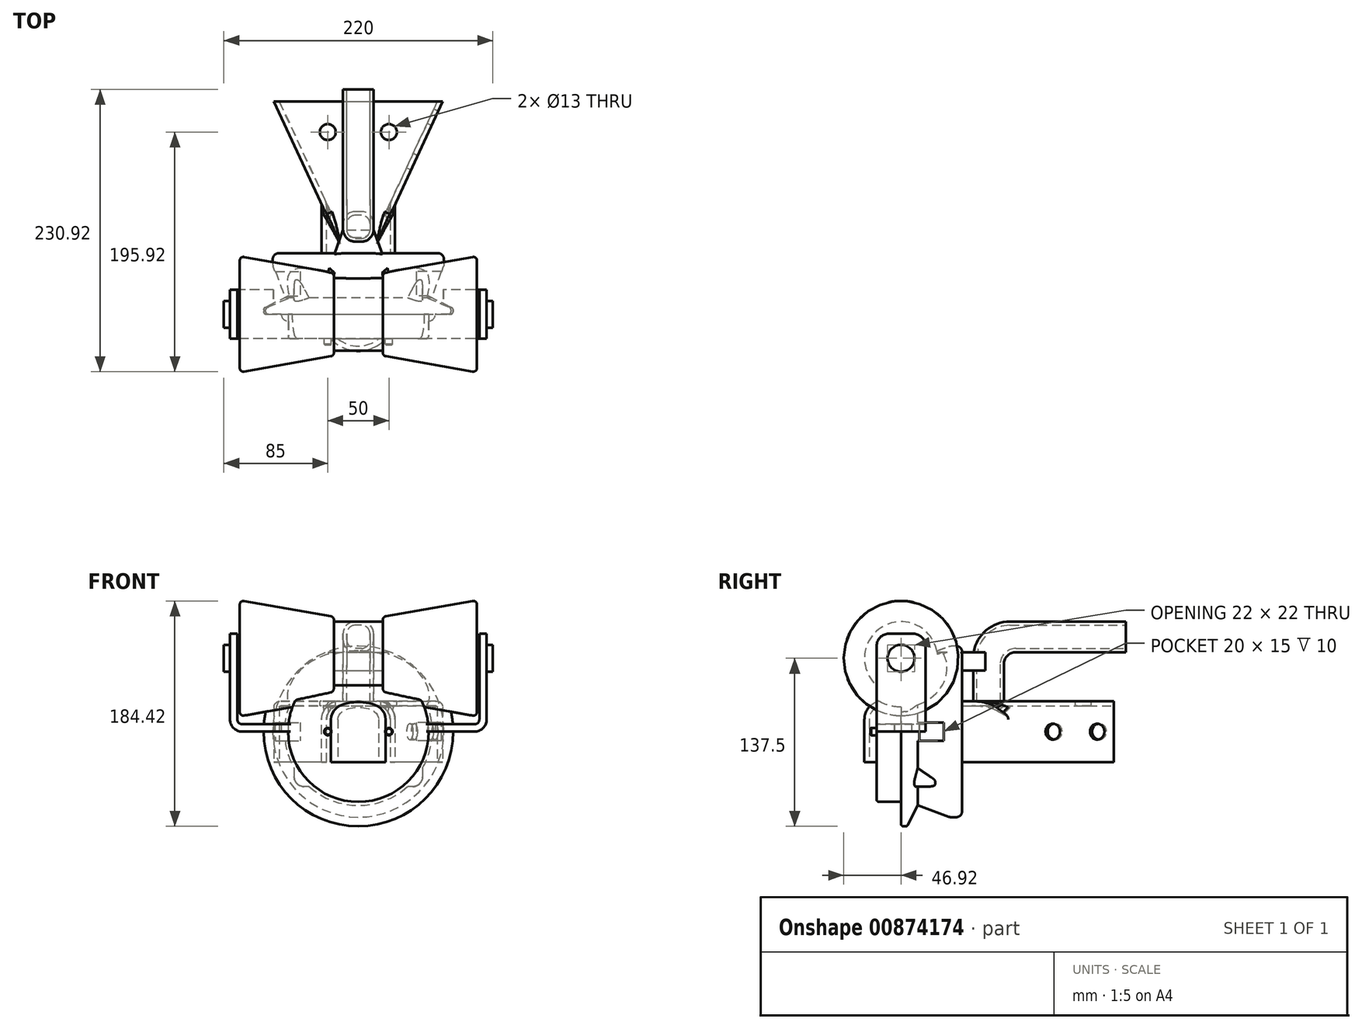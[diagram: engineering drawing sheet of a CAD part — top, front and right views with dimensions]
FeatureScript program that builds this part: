
annotation { "Feature Type Name" : "Feature", "Feature Type Description" : "" }
export const myFeature = defineFeature(function(context is Context, id is Id, definition is map)
    precondition{}
    {
        {
            var Q0;
            Q0=qCreatedBy(makeId("Front.planeOp"),FACE);
            var sketch = newSketch(context, id + "F0", { "sketchPlane" : qUnion([Q0])});
            skLineSegment(sketch, "E0.bottom", {"start": v(-52.5, -45) * mm, "end": v(52.5, -45) * mm});
            skLineSegment(sketch, "E0.top", {"start": v(-52.5, 45) * mm, "end": v(52.5, 45) * mm});
            skLineSegment(sketch, "E0.left", {"start": v(-52.5, -45) * mm, "end": v(-52.5, 45) * mm});
            skLineSegment(sketch, "E0.right", {"start": v(52.5, -45) * mm, "end": v(52.5, 45) * mm});
            skPoint(sketch, "E0.middle", {"position": v(0, 0) * mm});
            skSolve(sketch);
        }
        {
            var Q0;
            Q0 = qSketchRegion(id + "F0", true);
            extrude(context, id + "F1", {"entities" : qUnion([Q0]), "oppositeDirection" : true, "depth" : 30 * mm, "offsetDistance" : 25 * mm});
        }
        {
            var Q0;
            Q0=makeQuery(id+"F1.opExtrude","SWEPT_EDGE",EDGE,{"disambiguationData":[OSD([sQuery(id+"F0.wireOp",EDGE,"E0.top"),sQuery(id+"F0.wireOp",EDGE,"E0.right")])]});
            var Q1;
            Q1=makeQuery(id+"F1.opExtrude","SWEPT_EDGE",EDGE,{"disambiguationData":[OSD([sQuery(id+"F0.wireOp",EDGE,"E0.top"),sQuery(id+"F0.wireOp",EDGE,"E0.left")])]});
            var Q2;
            Q2=makeQuery(id+"F1.opExtrude","SWEPT_EDGE",EDGE,{"disambiguationData":[OSD([sQuery(id+"F0.wireOp",EDGE,"E0.bottom"),sQuery(id+"F0.wireOp",EDGE,"E0.right")])]});
            var Q3;
            Q3=makeQuery(id+"F1.opExtrude","SWEPT_EDGE",EDGE,{"disambiguationData":[OSD([sQuery(id+"F0.wireOp",EDGE,"E0.bottom"),sQuery(id+"F0.wireOp",EDGE,"E0.left")])]});
            fillet(context, id + "F2", {"entities" : qUnion([Q0, Q1, Q2, Q3]), "radius" : 8 * mm, "tangentPropagation" : true, "allowEdgeOverflow" : false});
        }
        {
            var Q0;
            Q0=makeQuery(id+"F1.opExtrude","CAP_EDGE",EDGE,{"disambiguationData":[OSD([sQuery(id+"F0.wireOp",EDGE,"E0.top")])],"isStart":false});
            fillet(context, id + "F3", {"entities" : qUnion([Q0]), "radius" : 3 * mm, "tangentPropagation" : true, "allowEdgeOverflow" : false});
        }
        {
            var Q0;
            Q0=qCreatedBy(makeId("Right.planeOp"),FACE);
            var sketch = newSketch(context, id + "F4", { "sketchPlane" : qUnion([Q0])});
            skLineSegment(sketch, "E1.bottom", {"start": v(20, 80) * mm, "end": v(-20, 80) * mm});
            skLineSegment(sketch, "E1.top", {"start": v(20, 0) * mm, "end": v(-20, 0) * mm});
            skLineSegment(sketch, "E1.left", {"start": v(20, 80) * mm, "end": v(20, 0) * mm});
            skLineSegment(sketch, "E1.right", {"start": v(-20, 80) * mm, "end": v(-20, 0) * mm});
            skSolve(sketch);
        }
        {
            var Q0;
            Q0 = qSketchRegion(id + "F4", true);
            extrude(context, id + "F5", {"entities" : qUnion([Q0]), "depth" : 210 * mm, "offsetDistance" : 25 * mm, "symmetric" : true});
        }
        {
            var Q0;
            Q0=makeQuery(id+"F5.opExtrude","CAP_EDGE",EDGE,{"disambiguationData":[OSD([sQuery(id+"F4.wireOp",EDGE,"E1.top")])],"isStart":false});
            var Q1;
            Q1=makeQuery(id+"F5.opExtrude","CAP_EDGE",EDGE,{"disambiguationData":[OSD([sQuery(id+"F4.wireOp",EDGE,"E1.top")])],"isStart":true});
            var Q2;
            Q2=makeQuery(id+"F5.opExtrude","SWEPT_EDGE",EDGE,{"disambiguationData":[OSD([sQuery(id+"F4.wireOp",EDGE,"E1.bottom"),sQuery(id+"F4.wireOp",EDGE,"E1.right")])]});
            var Q3;
            Q3=makeQuery(id+"F5.opExtrude","SWEPT_EDGE",EDGE,{"disambiguationData":[OSD([sQuery(id+"F4.wireOp",EDGE,"E1.bottom"),sQuery(id+"F4.wireOp",EDGE,"E1.left")])]});
            fillet(context, id + "F6", {"entities" : qUnion([Q0, Q1, Q2, Q3]), "radius" : 10 * mm, "tangentPropagation" : true, "allowEdgeOverflow" : false});
        }
        {
            var Q0;
            Q0=makeQuery(id+"F5.opExtrude","SWEPT_FACE",FACE,{"disambiguationData":[OSD([sQuery(id+"F4.wireOp",EDGE,"E1.right")])]});
            var Q1;
            Q1=makeQuery(id+"F6.opFillet","BLEND_FACE",FACE,{"disambiguationData":[OSD([sQuery(id+"F4.wireOp",EDGE,"E1.bottom"),sQuery(id+"F4.wireOp",EDGE,"E1.right")])]});
            var Q2;
            Q2=makeQuery(id+"F5.opExtrude","SWEPT_FACE",FACE,{"disambiguationData":[OSD([sQuery(id+"F4.wireOp",EDGE,"E1.bottom")])]});
            var Q3;
            Q3=makeQuery(id+"F6.opFillet","BLEND_FACE",FACE,{"disambiguationData":[OSD([sQuery(id+"F4.wireOp",EDGE,"E1.bottom"),sQuery(id+"F4.wireOp",EDGE,"E1.left")])]});
            var Q4;
            Q4=makeQuery(id+"F5.opExtrude","SWEPT_FACE",FACE,{"disambiguationData":[OSD([sQuery(id+"F4.wireOp",EDGE,"E1.left")])]});
            shell(context, id + "F7", {"entities" : qUnion([Q0, Q1, Q2, Q3, Q4]), "thickness" : 6 * mm});
        }
        {
            var Q0;
            Q0=makeQuery(id+"F5.opExtrude","SWEPT_FACE",FACE,{"disambiguationData":[OSD([sQuery(id+"F4.wireOp",EDGE,"E1.top")])]});
            var sketch = newSketch(context, id + "F8", { "sketchPlane" : qUnion([Q0])});
            skLineSegment(sketch, "E2.bottom", {"start": v(-42.5, -5.5) * mm, "end": v(-57.5, -5.5) * mm});
            skLineSegment(sketch, "E2.top", {"start": v(-42.5, 5.5) * mm, "end": v(-57.5, 5.5) * mm});
            skPoint(sketch, "E2.middle", {"position": v(-50, 0) * mm});
            skLineSegment(sketch, "E3.bottom", {"start": v(57.5, -5.5) * mm, "end": v(42.5, -5.5) * mm});
            skLineSegment(sketch, "E3.top", {"start": v(57.5, 5.5) * mm, "end": v(42.5, 5.5) * mm});
            skPoint(sketch, "E3.middle", {"position": v(50, 0) * mm});
            skArc(sketch, "E4", {"start": v(-57.5, 5.5) * mm, "mid": v(-63, 0) * mm, "end": v(-57.5, -5.5) * mm});
            skArc(sketch, "E5", {"start": v(-42.5, -5.5) * mm, "mid": v(-37, 0) * mm, "end": v(-42.5, 5.5) * mm});
            skArc(sketch, "E6", {"start": v(42.5, 5.5) * mm, "mid": v(37, 0) * mm, "end": v(42.5, -5.5) * mm});
            skArc(sketch, "E7", {"start": v(57.5, -5.5) * mm, "mid": v(63, 0) * mm, "end": v(57.5, 5.5) * mm});
            skSolve(sketch);
        }
        {
            var Q0;
            Q0 = qSketchRegion(id + "F8", true);
            extrude(context, id + "F9", {"entities" : qUnion([Q0]), "operationType" : NewBodyOperationType.REMOVE, "endBound" : BoundingType.THROUGH_ALL, "oppositeDirection" : true, "depth" : 25 * mm, "offsetDistance" : 25 * mm});
        }
        {
            var Q0;
            Q0=qCreatedBy(makeId("Right.planeOp"),FACE);
            var sketch = newSketch(context, id + "F10", { "sketchPlane" : qUnion([Q0])});
            skCircle(sketch, "E8", {"center": v(0, 60) * mm, "radius": 11 * mm});
            skSolve(sketch);
        }
        {
            var Q0;
            Q0 = qSketchRegion(id + "F10", true);
            extrude(context, id + "F11", {"entities" : qUnion([Q0]), "operationType" : NewBodyOperationType.REMOVE, "endBound" : BoundingType.THROUGH_ALL, "oppositeDirection" : true, "depth" : 25 * mm, "offsetDistance" : 25 * mm, "hasSecondDirection" : true, "secondDirectionBound" : BoundingType.THROUGH_ALL, "secondDirectionOppositeDirection" : false, "secondDirectionDepth" : 25 * mm});
        }
        {
            var Q0;
            Q0 = qSketchRegion(id + "F10", true);
            extrude(context, id + "F12", {"entities" : qUnion([Q0]), "operationType" : NewBodyOperationType.ADD, "depth" : 220 * mm, "offsetDistance" : 25 * mm, "symmetric" : true});
        }
        {
            var Q0;
            Q0=qCreatedBy(makeId("Front.planeOp"),FACE);
            var sketch = newSketch(context, id + "F13", { "sketchPlane" : qUnion([Q0])});
            skLineSegment(sketch, "E9", {"start": v(-99, 60) * mm, "end": v(99, 60) * mm, "construction": true});
            skLineSegment(sketch, "E10", {"start": v(97, 71) * mm, "end": v(-97, 71) * mm});
            skLineSegment(sketch, "E11", {"start": v(-97, 71) * mm, "end": v(-97, 107.5) * mm});
            skLineSegment(sketch, "E12", {"start": v(-97, 107.5) * mm, "end": v(-20, 93.92) * mm});
            skLineSegment(sketch, "E13", {"start": v(-20, 93.92) * mm, "end": v(-20, 89.92) * mm});
            skLineSegment(sketch, "E14", {"start": v(-20, 89.92) * mm, "end": v(20, 89.92) * mm});
            skLineSegment(sketch, "E15", {"start": v(20, 89.92) * mm, "end": v(20, 93.92) * mm});
            skLineSegment(sketch, "E16", {"start": v(20, 93.92) * mm, "end": v(97, 107.5) * mm});
            skLineSegment(sketch, "E17", {"start": v(97, 107.5) * mm, "end": v(97, 71) * mm});
            skSolve(sketch);
        }
        {
            var Q0;
            Q0 = qSketchRegion(id + "F13", true);
            var Q1;
            Q1=sQuery(id+"F13.wireOp",EDGE,"E9");
            revolve(context, id + "F14", {"surfaceOperationType" : NewSurfaceOperationType.NEW, "entities" : qUnion([Q0]), "axis" : qUnion([Q1]), "revolveType" : RevolveType.FULL});
        }
        {
            var Q0;
            Q0=makeQuery(id+"F14.opRevolve","SWEPT_EDGE",EDGE,{"disambiguationData":[OSD([sQuery(id+"F13.wireOp",EDGE,"E11"),sQuery(id+"F13.wireOp",EDGE,"E12")])]});
            var Q1;
            Q1=makeQuery(id+"F14.opRevolve","SWEPT_EDGE",EDGE,{"disambiguationData":[OSD([sQuery(id+"F13.wireOp",EDGE,"E16"),sQuery(id+"F13.wireOp",EDGE,"E17")])]});
            var Q2;
            Q2=makeQuery(id+"F14.opRevolve","SWEPT_EDGE",EDGE,{"disambiguationData":[OSD([sQuery(id+"F13.wireOp",EDGE,"E15"),sQuery(id+"F13.wireOp",EDGE,"E16")])]});
            var Q3;
            Q3=makeQuery(id+"F14.opRevolve","SWEPT_EDGE",EDGE,{"disambiguationData":[OSD([sQuery(id+"F13.wireOp",EDGE,"E12"),sQuery(id+"F13.wireOp",EDGE,"E13")])]});
            fillet(context, id + "F15", {"entities" : qUnion([Q0, Q1, Q2, Q3]), "radius" : 3 * mm, "tangentPropagation" : true, "allowEdgeOverflow" : false});
        }
        {
            var Q0;
            Q0=qCreatedBy(makeId("Right.planeOp"),FACE);
            var sketch = newSketch(context, id + "F16", { "sketchPlane" : qUnion([Q0])});
            skLineSegment(sketch, "E18", {"start": v(0, 0) * mm, "end": v(276.07, 0) * mm, "construction": true});
            skLineSegment(sketch, "E19", {"start": v(0, 0) * mm, "end": v(0, 55.44) * mm});
            skLineSegment(sketch, "E20", {"start": v(0, 55.44) * mm, "end": v(40, 70) * mm});
            skLineSegment(sketch, "E21", {"start": v(50, 70) * mm, "end": v(50, 0) * mm});
            skLineSegment(sketch, "E22", {"start": v(50, 0) * mm, "end": v(0, 0) * mm});
            skLineSegment(sketch, "E23", {"start": v(50, 70) * mm, "end": v(40, 70) * mm});
            skSolve(sketch);
        }
        {
            var Q0;
            Q0 = qSketchRegion(id + "F16", true);
            var Q1;
            Q1=sQuery(id+"F16.wireOp",EDGE,"E18");
            revolve(context, id + "F17", {"surfaceOperationType" : NewSurfaceOperationType.NEW, "entities" : qUnion([Q0]), "axis" : qUnion([Q1]), "revolveType" : RevolveType.FULL});
        }
        {
            var Q0;
            Q0=makeQuery(id+"F17.opRevolve","SWEPT_EDGE",EDGE,{"disambiguationData":[OSD([sQuery(id+"F16.wireOp",EDGE,"E21"),sQuery(id+"F16.wireOp",EDGE,"E23")])]});
            var Q1;
            Q1=makeQuery(id+"F17.opRevolve","SWEPT_EDGE",EDGE,{"disambiguationData":[OSD([sQuery(id+"F16.wireOp",EDGE,"E20"),sQuery(id+"F16.wireOp",EDGE,"E23")])]});
            var Q2;
            Q2=makeQuery(id+"F17.opRevolve","SWEPT_EDGE",EDGE,{"disambiguationData":[OSD([sQuery(id+"F16.wireOp",EDGE,"E19"),sQuery(id+"F16.wireOp",EDGE,"E20")])]});
            fillet(context, id + "F18", {"entities" : qUnion([Q0, Q1, Q2]), "radius" : 5 * mm, "tangentPropagation" : true, "allowEdgeOverflow" : false});
        }
        {
            var Q0;
            Q0=makeQuery(id+"F17.opRevolve","SWEPT_FACE",FACE,{"disambiguationData":[OSD([sQuery(id+"F16.wireOp",EDGE,"E19")])]});
            var sketch = newSketch(context, id + "F19", { "sketchPlane" : qUnion([Q0])});
            skLineSegment(sketch, "E24", {"start": v(0, 0) * mm, "end": v(0, 51.94) * mm, "construction": true});
            skCircle(sketch, "E25", {"center": v(-25, 0) * mm, "radius": 3 * mm});
            skCircle(sketch, "E26", {"center": v(25, 0) * mm, "radius": 3 * mm});
            skSolve(sketch);
        }
        {
            var Q0;
            Q0 = qSketchRegion(id + "F19", true);
            extrude(context, id + "F20", {"entities" : qUnion([Q0]), "operationType" : NewBodyOperationType.ADD, "depth" : 25 * mm, "offsetDistance" : 25 * mm});
        }
        {
            var Q0;
            Q0=makeQuery(id+"F20.opExtrude","CAP_EDGE",EDGE,{"disambiguationData":[OSD([sQuery(id+"F19.wireOp",EDGE,"E25")])],"isStart":false});
            var Q1;
            Q1=makeQuery(id+"F20.opExtrude","CAP_EDGE",EDGE,{"disambiguationData":[OSD([sQuery(id+"F19.wireOp",EDGE,"E26")])],"isStart":false});
            chamfer(context, id + "F21", {"entities" : qUnion([Q0, Q1]), "width" : .5 * mm, "tangentPropagation" : true});
        }
        {
            var Q0;
            Q0=makeQuery(id+"F17.opRevolve","SWEPT_FACE",FACE,{"disambiguationData":[OSD([sQuery(id+"F16.wireOp",EDGE,"E19")])]});
            var sketch = newSketch(context, id + "F22", { "sketchPlane" : qUnion([Q0])});
            skLineSegment(sketch, "E27", {"start": v(-87.7, 0) * mm, "end": v(88.28, 0) * mm, "construction": true});
            skArc(sketch, "E28.0", {"start": v(-69.3, 7.5) * mm, "mid": v(-69.7, 0) * mm, "end": v(-69.3, -7.5) * mm});
            skLineSegment(sketch, "E29.bottom", {"start": v(-69.3, 7.5) * mm, "end": v(-47.5, 7.5) * mm});
            skLineSegment(sketch, "E29.top", {"start": v(-69.3, -7.5) * mm, "end": v(-47.5, -7.5) * mm});
            skLineSegment(sketch, "E29.right", {"start": v(-47.5, 7.5) * mm, "end": v(-47.5, -7.5) * mm});
            skPoint(sketch, "E29.middle", {"position": v(-58.4, 0) * mm});
            skLineSegment(sketch, "E30.bottom", {"start": v(69.3, 7.5) * mm, "end": v(47.5, 7.5) * mm});
            skLineSegment(sketch, "E30.top", {"start": v(69.3, -7.5) * mm, "end": v(47.5, -7.5) * mm});
            skLineSegment(sketch, "E30.right", {"start": v(47.5, 7.5) * mm, "end": v(47.5, -7.5) * mm});
            skPoint(sketch, "E30.middle", {"position": v(58.4, 0) * mm});
            skLineSegment(sketch, "E31", {"start": v(0, 0) * mm, "end": v(0, 85.87) * mm, "construction": true});
            skArc(sketch, "E32.trimOffspring", {"start": v(69.3, -7.5) * mm, "mid": v(51.87, 46.56) * mm, "end": v(0, 69.7) * mm});
            skSolve(sketch);
        }
        {
            var Q0;
            Q0 = qSketchRegion(id + "F22", true);
            extrude(context, id + "F23", {"entities" : qUnion([Q0]), "operationType" : NewBodyOperationType.REMOVE, "oppositeDirection" : true, "depth" : 35 * mm, "offsetDistance" : 25 * mm});
        }
        {
            var Q0;
            Q0=qCreatedBy(makeId("Right.planeOp"),FACE);
            var sketch = newSketch(context, id + "F24", { "sketchPlane" : qUnion([Q0])});
            skLineSegment(sketch, "E33", {"start": v(-114.02, 0) * mm, "end": v(0, 0) * mm, "construction": true});
            skLineSegment(sketch, "E34", {"start": v(0, 57.5) * mm, "end": v(0, 77.5) * mm});
            skLineSegment(sketch, "E35", {"start": v(0, 77.5) * mm, "end": v(5, 77.5) * mm});
            skLineSegment(sketch, "E36", {"start": v(5, 77.5) * mm, "end": v(15, 57.5) * mm});
            skLineSegment(sketch, "E37", {"start": v(15, 57.5) * mm, "end": v(15, 35.26) * mm});
            skLineSegment(sketch, "E38", {"start": v(12, 0) * mm, "end": v(-20, 0) * mm});
            skLineSegment(sketch, "E39", {"start": v(-20, 0) * mm, "end": v(-20, 57.5) * mm});
            skLineSegment(sketch, "E40", {"start": v(-20, 57.5) * mm, "end": v(0, 57.5) * mm});
            skLineSegment(sketch, "E41", {"start": v(15, 35.26) * mm, "end": v(12, 35) * mm});
            skLineSegment(sketch, "E42", {"start": v(12, 35) * mm, "end": v(12, 0) * mm});
            skPoint(sketch, "E43.orphan", {"position": v(15, 0) * mm});
            skSolve(sketch);
        }
        {
            var Q0;
            Q0 = qSketchRegion(id + "F24", true);
            var Q1;
            Q1=sQuery(id+"F24.wireOp",EDGE,"E33");
            revolve(context, id + "F25", {"surfaceOperationType" : NewSurfaceOperationType.NEW, "entities" : qUnion([Q0]), "axis" : qUnion([Q1]), "revolveType" : RevolveType.FULL});
        }
        {
            var Q0;
            Q0=makeQuery(id+"F25.opRevolve","SWEPT_FACE",FACE,{"disambiguationData":[OSD([sQuery(id+"F24.wireOp",EDGE,"E42")])]});
            var Q1;
            Q1=makeQuery(id+"F25.opRevolve","SWEPT_FACE",FACE,{"disambiguationData":[OSD([sQuery(id+"F24.wireOp",EDGE,"E37")])]});
            extrude(context, id + "F26", {"entities" : qUnion([Q0]), "operationType" : NewBodyOperationType.ADD, "endBound" : BoundingType.UP_TO_SURFACE, "depth" : 3 * mm, "endBoundEntityFace" : qUnion([Q1]), "offsetDistance" : 25 * mm});
        }
        {
            var Q0;
            Q0=makeQuery(id+"F25.opRevolve","SWEPT_EDGE",EDGE,{"disambiguationData":[OSD([sQuery(id+"F24.wireOp",EDGE,"E35"),sQuery(id+"F24.wireOp",EDGE,"E36")])]});
            var Q1;
            Q1=makeQuery(id+"F25.opRevolve","SWEPT_EDGE",EDGE,{"disambiguationData":[OSD([sQuery(id+"F24.wireOp",EDGE,"E34"),sQuery(id+"F24.wireOp",EDGE,"E35")])]});
            var Q2;
            Q2=makeQuery(id+"F25.opRevolve","SWEPT_EDGE",EDGE,{"disambiguationData":[OSD([sQuery(id+"F24.wireOp",EDGE,"E39"),sQuery(id+"F24.wireOp",EDGE,"E40")])]});
            var Q3;
            Q3=makeQuery(id+"F25.opRevolve","SWEPT_EDGE",EDGE,{"disambiguationData":[OSD([sQuery(id+"F24.wireOp",EDGE,"E34"),sQuery(id+"F24.wireOp",EDGE,"E40")])]});
            fillet(context, id + "F27", {"entities" : qUnion([Q0, Q1, Q2, Q3]), "radius" : 2 * mm, "tangentPropagation" : true, "allowEdgeOverflow" : false});
        }
        {
            var Q0;
            Q0=qCreatedBy(makeId("Top.planeOp"),FACE);
            var sketch = newSketch(context, id + "F28", { "sketchPlane" : qUnion([Q0])});
            skArc(sketch, "E44", {"start": v(-30, 0) * mm, "mid": v(0, -30) * mm, "end": v(30, 0) * mm});
            skLineSegment(sketch, "E45", {"start": v(0, 0) * mm, "end": v(0, 174) * mm, "construction": true});
            skLineSegment(sketch, "E46", {"start": v(-30, 0) * mm, "end": v(-30, 90) * mm});
            skLineSegment(sketch, "E47", {"start": v(-30, 90) * mm, "end": v(-69, 174) * mm});
            skLineSegment(sketch, "E48", {"start": v(-69, 174) * mm, "end": v(69, 174) * mm});
            skLineSegment(sketch, "E49", {"start": v(69, 174) * mm, "end": v(30, 90) * mm});
            skLineSegment(sketch, "E50", {"start": v(30, 90) * mm, "end": v(30, 0) * mm});
            skSolve(sketch);
        }
        {
            var Q0;
            Q0 = qSketchRegion(id + "F28", true);
            extrude(context, id + "F29", {"entities" : qUnion([Q0]), "depth" : 50 * mm, "offsetDistance" : 25 * mm, "symmetric" : true});
        }
        {
            var Q0;
            Q0=makeQuery(id+"F29.opExtrude","CAP_EDGE",EDGE,{"disambiguationData":[OSD([sQuery(id+"F28.wireOp",EDGE,"E44")])],"isStart":false});
            fillet(context, id + "F30", {"entities" : qUnion([Q0]), "radius" : 15 * mm, "tangentPropagation" : true, "allowEdgeOverflow" : false});
        }
        {
            var Q0;
            Q0=makeQuery(id+"F29.opExtrude","CAP_EDGE",EDGE,{"disambiguationData":[OSD([sQuery(id+"F28.wireOp",EDGE,"E49")])],"isStart":false});
            var Q1;
            Q1=makeQuery(id+"F29.opExtrude","CAP_EDGE",EDGE,{"disambiguationData":[OSD([sQuery(id+"F28.wireOp",EDGE,"E47")])],"isStart":false});
            fillet(context, id + "F31", {"entities" : qUnion([Q0, Q1]), "radius" : 5 * mm, "tangentPropagation" : true, "allowEdgeOverflow" : false});
        }
        {
            var Q0;
            Q0=makeQuery(id+"F29.opExtrude","SWEPT_EDGE",EDGE,{"disambiguationData":[OSD([sQuery(id+"F28.wireOp",EDGE,"E49"),sQuery(id+"F28.wireOp",EDGE,"E50")])]});
            var Q1;
            Q1=makeQuery(id+"F29.opExtrude","SWEPT_EDGE",EDGE,{"disambiguationData":[OSD([sQuery(id+"F28.wireOp",EDGE,"E46"),sQuery(id+"F28.wireOp",EDGE,"E47")])]});
            fillet(context, id + "F32", {"entities" : qUnion([Q0, Q1]), "radius" : 10 * mm, "tangentPropagation" : true, "allowEdgeOverflow" : false});
        }
        {
            var Q0;
            Q0=makeQuery(id+"F29.opExtrude","CAP_FACE",FACE,{"disambiguationData":[OSD([sQuery(id+"F28.wireOp",EDGE,"E44"),sQuery(id+"F28.wireOp",EDGE,"E46"),sQuery(id+"F28.wireOp",EDGE,"E47"),sQuery(id+"F28.wireOp",EDGE,"E48"),sQuery(id+"F28.wireOp",EDGE,"E49"),sQuery(id+"F28.wireOp",EDGE,"E50")])],"isStart":true});
            var Q1;
            Q1=makeQuery(id+"F29.opExtrude","SWEPT_FACE",FACE,{"disambiguationData":[OSD([sQuery(id+"F28.wireOp",EDGE,"E48")])]});
            shell(context, id + "F33", {"entities" : qUnion([Q0, Q1]), "thickness" : 4 * mm});
        }
        {
            var Q0;
            Q0=qCreatedBy(makeId("Right.planeOp"),FACE);
            var sketch = newSketch(context, id + "F34", { "sketchPlane" : qUnion([Q0])});
            skLineSegment(sketch, "E51", {"start": v(84, 25) * mm, "end": v(84, 55) * mm});
            skLineSegment(sketch, "E52", {"start": v(94, 65) * mm, "end": v(184, 65) * mm});
            skLineSegment(sketch, "E53", {"start": v(184, 65) * mm, "end": v(184, 90) * mm});
            skLineSegment(sketch, "E54", {"start": v(184, 90) * mm, "end": v(89, 90) * mm});
            skLineSegment(sketch, "E55", {"start": v(59, 60) * mm, "end": v(59, 25) * mm});
            skLineSegment(sketch, "E56", {"start": v(59, 25) * mm, "end": v(84, 25) * mm});
            skPoint(sketch, "E57.visualSharp", {"position": v(59, 90) * mm});
            skArc(sketch, "E57.filletArc", {"start": v(89, 90) * mm, "mid": v(67.79, 81.21) * mm, "end": v(59, 60) * mm});
            skPoint(sketch, "E58.visualSharp", {"position": v(84, 65) * mm});
            skArc(sketch, "E58.filletArc", {"start": v(94, 65) * mm, "mid": v(86.93, 62.07) * mm, "end": v(84, 55) * mm});
            skSolve(sketch);
        }
        {
            var Q0;
            Q0 = qSketchRegion(id + "F34", true);
            extrude(context, id + "F35", {"entities" : qUnion([Q0]), "operationType" : NewBodyOperationType.ADD, "depth" : 25 * mm, "offsetDistance" : 25 * mm, "symmetric" : true});
        }
        {
            var Q0;
            Q0=makeQuery(id+"F35.opExtrude","CAP_EDGE",EDGE,{"disambiguationData":[OSD([sQuery(id+"F34.wireOp",EDGE,"E52")])],"isStart":false});
            var Q1;
            Q1=makeQuery(id+"F35.opExtrude","CAP_EDGE",EDGE,{"disambiguationData":[OSD([sQuery(id+"F34.wireOp",EDGE,"E54")])],"isStart":false});
            var Q2;
            Q2=makeQuery(id+"F35.opExtrude","CAP_EDGE",EDGE,{"disambiguationData":[OSD([sQuery(id+"F34.wireOp",EDGE,"E54")])],"isStart":true});
            var Q3;
            Q3=makeQuery(id+"F35.opExtrude","CAP_EDGE",EDGE,{"disambiguationData":[OSD([sQuery(id+"F34.wireOp",EDGE,"E52")])],"isStart":true});
            fillet(context, id + "F36", {"entities" : qUnion([Q0, Q1, Q2, Q3]), "radius" : 10 * mm, "tangentPropagation" : true, "allowEdgeOverflow" : false});
        }
        {
            var Q0;
            Q0=makeQuery(id+"F35.opExtrude","SWEPT_FACE",FACE,{"disambiguationData":[OSD([sQuery(id+"F34.wireOp",EDGE,"E53")])]});
            shell(context, id + "F37", {"entities" : qUnion([Q0]), "thickness" : 3 * mm});
        }
        {
            var Q0;
            Q0=makeQuery(id+"F29.opExtrude","CAP_FACE",FACE,{"disambiguationData":[OSD([sQuery(id+"F28.wireOp",EDGE,"E44"),sQuery(id+"F28.wireOp",EDGE,"E46"),sQuery(id+"F28.wireOp",EDGE,"E47"),sQuery(id+"F28.wireOp",EDGE,"E48"),sQuery(id+"F28.wireOp",EDGE,"E49"),sQuery(id+"F28.wireOp",EDGE,"E50")])],"isStart":false});
            var sketch = newSketch(context, id + "F38", { "sketchPlane" : qUnion([Q0])});
            skLineSegment(sketch, "E59", {"start": v(0, 0) * mm, "end": v(0, 149) * mm, "construction": true});
            skLineSegment(sketch, "E60", {"start": v(-25, 149) * mm, "end": v(25, 149) * mm, "construction": true});
            skCircle(sketch, "E61", {"center": v(-25, 149) * mm, "radius": 6.5 * mm});
            skCircle(sketch, "E62", {"center": v(25, 149) * mm, "radius": 6.5 * mm});
            skSolve(sketch);
        }
        {
            var Q0;
            Q0 = qSketchRegion(id + "F38", true);
            extrude(context, id + "F39", {"entities" : qUnion([Q0]), "operationType" : NewBodyOperationType.REMOVE, "endBound" : BoundingType.THROUGH_ALL, "oppositeDirection" : true, "depth" : 25 * mm, "offsetDistance" : 25 * mm});
        }
        {
            var Q0;
            Q0=makeQuery(id+"F29.opExtrude","SWEPT_FACE",FACE,{"disambiguationData":[OSD([sQuery(id+"F28.wireOp",EDGE,"E49")])]});
            var sketch = newSketch(context, id + "F40", { "sketchPlane" : qUnion([Q0])});
            skCircle(sketch, "E63", {"center": v(171.88, 0) * mm, "radius": 6.5 * mm});
            skCircle(sketch, "E64", {"center": v(131.88, 0) * mm, "radius": 6.5 * mm});
            skLineSegment(sketch, "E65", {"start": v(131.88, 0) * mm, "end": v(171.88, 0) * mm, "construction": true});
            skSolve(sketch);
        }
        {
            var Q0;
            Q0 = qSketchRegion(id + "F40", true);
            extrude(context, id + "F41", {"entities" : qUnion([Q0]), "operationType" : NewBodyOperationType.REMOVE, "endBound" : BoundingType.UP_TO_NEXT, "oppositeDirection" : true, "depth" : 25 * mm, "offsetDistance" : 25 * mm});
        }
        {
            var Q0;
            Q0=makeQuery(id+"F29.opExtrude","CAP_FACE",FACE,{"disambiguationData":[OSD([sQuery(id+"F28.wireOp",EDGE,"E44"),sQuery(id+"F28.wireOp",EDGE,"E46"),sQuery(id+"F28.wireOp",EDGE,"E47"),sQuery(id+"F28.wireOp",EDGE,"E48"),sQuery(id+"F28.wireOp",EDGE,"E49"),sQuery(id+"F28.wireOp",EDGE,"E50")])],"isStart":false});
            cPlane(context, id + "F42", {"entities" : qUnion([Q0]), "cplaneType" : CPlaneType.OFFSET, "offset" : 25 * mm, "width" : 150 * mm, "height" : 150 * mm});
        }
        {
            var Q0;
            Q0=qCreatedBy(id+"F42.planeOp",FACE);
            var Q1;
            Q1=qCreatedBy(id+"F42.planeOp",FACE);
            var sketch = newSketch(context, id + "F43", { "sketchPlane" : qUnion([Q0, Q1])});
            skArc(sketch, "E66", {"start": v(-23.51, 38.49) * mm, "mid": v(0, 5) * mm, "end": v(23.51, 38.49) * mm});
            skCircle(sketch, "E67", {"center": v(0, 30) * mm, "radius": 20 * mm});
            skLineSegment(sketch, "E68", {"start": v(-23.51, 38.49) * mm, "end": v(-12.5, 69) * mm});
            skLineSegment(sketch, "E69", {"start": v(-12.5, 69) * mm, "end": v(12.5, 69) * mm});
            skLineSegment(sketch, "E70", {"start": v(12.5, 69) * mm, "end": v(23.51, 38.49) * mm});
            skSolve(sketch);
        }
        {
            var Q0;
            Q0 = qSketchRegion(id + "F43", true);
            extrude(context, id + "F44", {"entities" : qUnion([Q0]), "operationType" : NewBodyOperationType.ADD, "depth" : 15 * mm, "offsetDistance" : 25 * mm});
        }
    });
